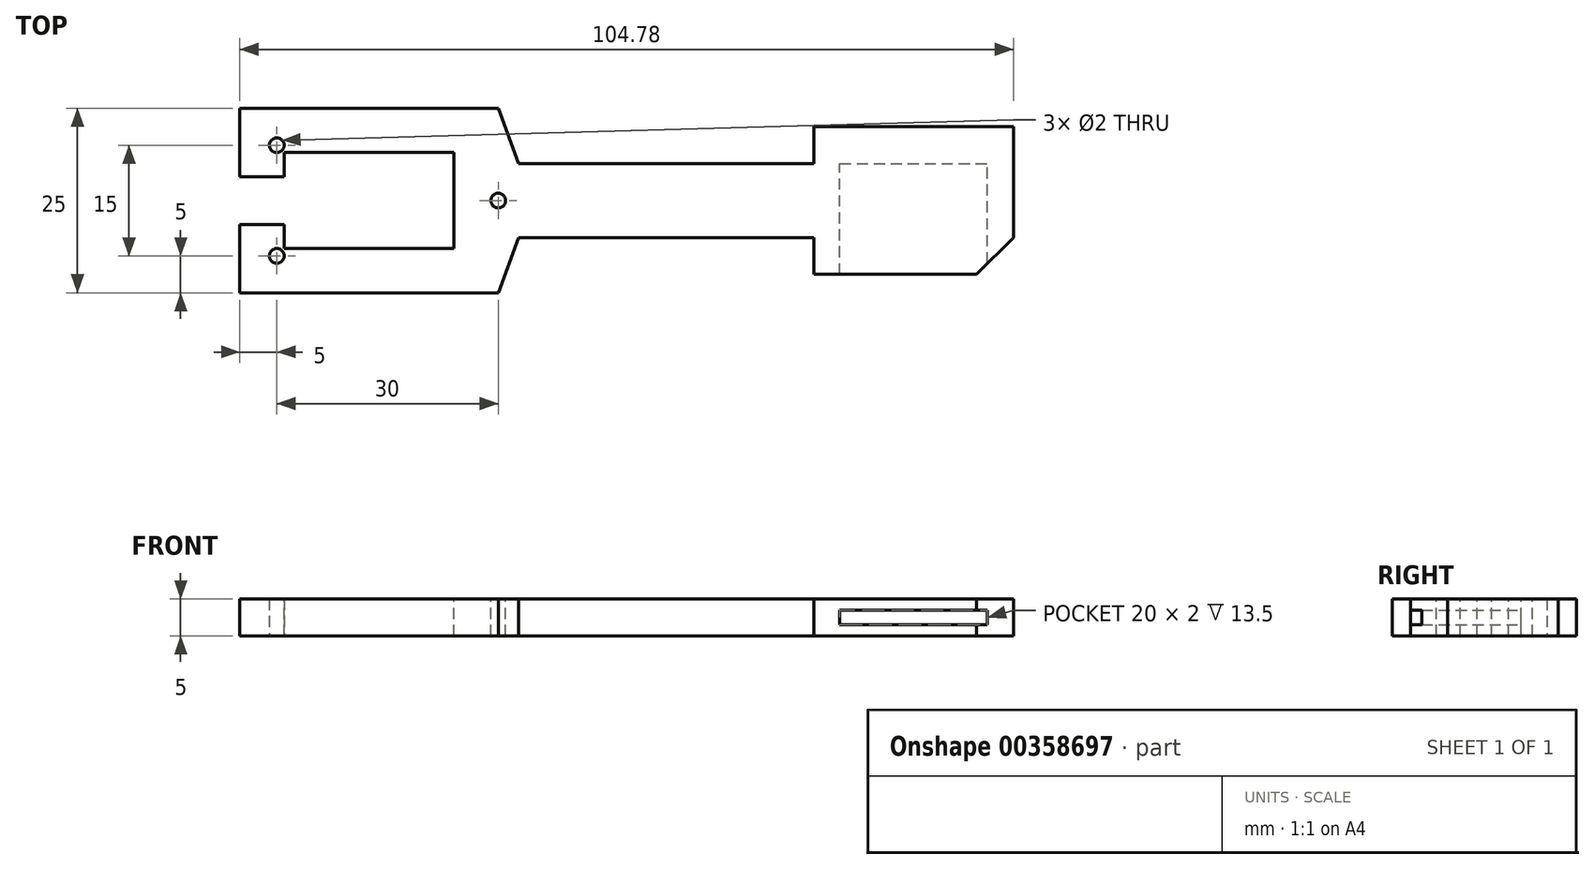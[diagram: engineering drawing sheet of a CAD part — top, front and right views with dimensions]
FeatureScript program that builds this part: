
annotation { "Feature Type Name" : "Feature", "Feature Type Description" : "" }
export const myFeature = defineFeature(function(context is Context, id is Id, definition is map)
    precondition{}
    {
        {
            var Q0;
            Q0=qCreatedBy(makeId("Top.planeOp"),FACE);
            var sketch = newSketch(context, id + "F0", { "sketchPlane" : qUnion([Q0])});
            skLineSegment(sketch, "E0.bottom", {"start": v(0, 0) * mm, "end": v(-35, 0) * mm});
            skLineSegment(sketch, "E0.top", {"start": v(0, 25) * mm, "end": v(-35, 25) * mm});
            skLineSegment(sketch, "E0.right", {"start": v(-35, 0) * mm, "end": v(-35, 25) * mm});
            skPoint(sketch, "E0.middle", {"position": v(-17.5, 12.5) * mm});
            skLineSegment(sketch, "E1.bottom", {"start": v(-29, 6) * mm, "end": v(-6, 6) * mm});
            skLineSegment(sketch, "E1.top", {"start": v(-29, 19) * mm, "end": v(-6, 19) * mm});
            skLineSegment(sketch, "E1.left", {"start": v(-29, 6) * mm, "end": v(-29, 19) * mm});
            skLineSegment(sketch, "E1.right", {"start": v(-6, 6) * mm, "end": v(-6, 19) * mm});
            skLineSegment(sketch, "E2", {"start": v(0, 25) * mm, "end": v(2.78, 17.5) * mm});
            skLineSegment(sketch, "E3", {"start": v(0, 0) * mm, "end": v(2.78, 7.5) * mm});
            skLineSegment(sketch, "E4", {"start": v(-17.5, 25) * mm, "end": v(-17.5, 19) * mm, "construction": true});
            skLineSegment(sketch, "E5", {"start": v(-17.5, 19) * mm, "end": v(-17.5, 12.5) * mm, "construction": true});
            skLineSegment(sketch, "E6", {"start": v(-17.5, 6) * mm, "end": v(-17.5, 0) * mm, "construction": true});
            skLineSegment(sketch, "E7", {"start": v(-17.5, 12.5) * mm, "end": v(-17.5, 6) * mm, "construction": true});
            skLineSegment(sketch, "E8", {"start": v(-6, 12.5) * mm, "end": v(2.78, 12.5) * mm, "construction": true});
            skLineSegment(sketch, "E9", {"start": v(2.78, 17.5) * mm, "end": v(42.78, 17.5) * mm});
            skLineSegment(sketch, "E10", {"start": v(42.78, 17.5) * mm, "end": v(42.78, 7.5) * mm});
            skLineSegment(sketch, "E11", {"start": v(42.78, 7.5) * mm, "end": v(2.78, 7.5) * mm});
            skLineSegment(sketch, "E12", {"start": v(2.78, 17.5) * mm, "end": v(2.78, 7.5) * mm});
            skLineSegment(sketch, "E13", {"start": v(42.78, 7.5) * mm, "end": v(42.78, 2.5) * mm});
            skLineSegment(sketch, "E14", {"start": v(42.78, 2.5) * mm, "end": v(64.78, 2.5) * mm});
            skLineSegment(sketch, "E15", {"start": v(64.78, 2.5) * mm, "end": v(69.78, 7.5) * mm});
            skLineSegment(sketch, "E16", {"start": v(69.78, 7.5) * mm, "end": v(69.78, 17.5) * mm});
            skLineSegment(sketch, "E17", {"start": v(42.78, 17.5) * mm, "end": v(42.78, 22.5) * mm});
            skLineSegment(sketch, "E18", {"start": v(42.78, 22.5) * mm, "end": v(69.78, 22.5) * mm});
            skLineSegment(sketch, "E19", {"start": v(69.78, 22.5) * mm, "end": v(69.78, 17.5) * mm});
            skLineSegment(sketch, "E20", {"start": v(42.78, 17.5) * mm, "end": v(57.78, 17.5) * mm});
            skLineSegment(sketch, "E21", {"start": v(57.78, 17.5) * mm, "end": v(57.78, 2.5) * mm});
            skLineSegment(sketch, "E22", {"start": v(57.78, 17.5) * mm, "end": v(57.78, 22.5) * mm});
            skLineSegment(sketch, "E23", {"start": v(57.78, 17.5) * mm, "end": v(69.78, 17.5) * mm});
            skPoint(sketch, "E24", {"position": v(-30, 20) * mm});
            skPoint(sketch, "E25", {"position": v(-30, 5) * mm});
            skLineSegment(sketch, "E26", {"start": v(-29, 15.75) * mm, "end": v(-35, 15.75) * mm});
            skPoint(sketch, "E26.startSnap0", {"position": v(-17.5, 15.75) * mm});
            skLineSegment(sketch, "E27", {"start": v(-29, 9.25) * mm, "end": v(-35, 9.25) * mm});
            skLineSegment(sketch, "E28", {"start": v(-29, 9.25) * mm, "end": v(-17.5, 9.25) * mm});
            skPoint(sketch, "E29", {"position": v(0, 12.5) * mm});
            skSolve(sketch);
        }
        {
            var Q0;
            Q0=makeQuery(id+"F0.imprint","IMPRINT",FACE,{"disambiguationData":[TD([[makeQuery(id+"F0.imprint","IMPRINT",EDGE,{"derivedFrom":sQuery(id+"F0.wireOp",EDGE,"E0.bottom")}),-1.0]])]});
            var Q1;
            Q1=makeQuery(id+"F0.imprint","IMPRINT",FACE,{"disambiguationData":[TD([[makeQuery(id+"F0.imprint","IMPRINT",EDGE,{"derivedFrom":sQuery(id+"F0.wireOp",EDGE,"E9")}),-1.0]])]});
            extrude(context, id + "F1", {"entities" : qUnion([Q0, Q1]), "oppositeDirection" : true, "depth" : 5 * mm, "symmetric" : true});
        }
        {
            var Q0;
            {var subQ0=sQuery(id+"F0.wireOp",EDGE,"E17");Q0=makeQuery(id+"F0.imprint","IMPRINT",FACE,{"disambiguationData":[TD([[makeQuery(id+"F0.imprint","IMPRINT",EDGE,{"derivedFrom":subQ0}),-1.0]])]});}
            var Q1;
            {var subQ0=sQuery(id+"F0.wireOp",EDGE,"E19");Q1=makeQuery(id+"F0.imprint","IMPRINT",FACE,{"disambiguationData":[TD([[makeQuery(id+"F0.imprint","IMPRINT",EDGE,{"derivedFrom":subQ0}),-1.0]])]});}
            var Q2;
            {var subQ1=sQuery(id+"F0.wireOp",EDGE,"E15");Q2=makeQuery(id+"F0.imprint","IMPRINT",FACE,{"disambiguationData":[TD([[makeQuery(id+"F0.imprint","IMPRINT",EDGE,{"derivedFrom":subQ1}),1.0]])]});}
            var Q3;
            Q3=makeQuery(id+"F0.imprint","IMPRINT",FACE,{"disambiguationData":[TD([[makeQuery(id+"F0.imprint","IMPRINT",EDGE,{"derivedFrom":sQuery(id+"F0.wireOp",EDGE,"E10")}),1.0]])]});
            extrude(context, id + "F2", {"entities" : qUnion([Q0, Q1, Q2, Q3]), "operationType" : NewBodyOperationType.ADD, "oppositeDirection" : true, "depth" : 5 * mm, "symmetric" : true});
        }
        {
            var Q0;
            Q0=makeQuery(id+"F2.opExtrude","SWEPT_FACE",FACE,{"disambiguationData":[OSD([sQuery(id+"F0.wireOp",EDGE,"E18")])]});
            var sketch = newSketch(context, id + "F3", { "sketchPlane" : qUnion([Q0])});
            skLineSegment(sketch, "E30.0.0", {"start": v(-42.78, 2.5) * mm, "end": v(-69.78, 2.5) * mm});
            skLineSegment(sketch, "E30.0.1", {"start": v(-69.78, 2.5) * mm, "end": v(-69.78, -2.5) * mm});
            skLineSegment(sketch, "E30.0.2", {"start": v(-69.78, -2.5) * mm, "end": v(-42.78, -2.5) * mm});
            skLineSegment(sketch, "E30.0.3", {"start": v(-42.78, -2.5) * mm, "end": v(-42.78, 2.5) * mm});
            skLineSegment(sketch, "E31.0", {"start": v(-46.28, -1) * mm, "end": v(-66.28, -1) * mm});
            skLineSegment(sketch, "E31.1", {"start": v(-46.28, -1) * mm, "end": v(-46.28, 1) * mm});
            skLineSegment(sketch, "E31.2", {"start": v(-66.28, 1) * mm, "end": v(-46.28, 1) * mm});
            skLineSegment(sketch, "E31.3", {"start": v(-66.28, 1) * mm, "end": v(-66.28, -1) * mm});
            skSolve(sketch);
        }
        {
            var Q0;
            Q0=makeQuery(id+"F3.imprint","IMPRINT",FACE,{"disambiguationData":[TD([[makeQuery(id+"F3.imprint","IMPRINT",EDGE,{"derivedFrom":sQuery(id+"F3.wireOp",EDGE,"E31.0")}),-1.0]])]});
            extrude(context, id + "F4", {"entities" : qUnion([Q0]), "operationType" : NewBodyOperationType.REMOVE, "oppositeDirection" : true, "depth" : 25 * mm});
        }
        {
            var Q0;
            Q0=sQuery(id+"F0.wireOp",VERTEX,"E24");
            var Q1;
            Q1=sQuery(id+"F0.wireOp",VERTEX,"E25");
            var Q2;
            Q2=makeQuery(id+"F1.opExtrude","SWEPT_BODY",BODY,{"disambiguationData":[OSD([sQuery(id+"F0.wireOp",EDGE,"E0.bottom"),sQuery(id+"F0.wireOp",EDGE,"E0.top"),sQuery(id+"F0.wireOp",EDGE,"E0.right"),sQuery(id+"F0.wireOp",EDGE,"E1.bottom"),sQuery(id+"F0.wireOp",EDGE,"E1.top"),sQuery(id+"F0.wireOp",EDGE,"E1.left"),sQuery(id+"F0.wireOp",EDGE,"E1.right"),sQuery(id+"F0.wireOp",EDGE,"E2"),sQuery(id+"F0.wireOp",EDGE,"E3"),sQuery(id+"F0.wireOp",EDGE,"E9"),sQuery(id+"F0.wireOp",EDGE,"E10"),sQuery(id+"F0.wireOp",EDGE,"E11")])]});
            hole(context, id + "F5", {"style" : HoleStyle.SIMPLE, "endStyle" : HoleEndStyle.BLIND, "oppositeDirection" : true, "holeDiameter" : 2 * mm, "holeDepth" : 30 * mm, "isTappedThrough" : true, "tappedDepth" : 12 * mm, "tapClearance" : 3, "locations" : qUnion([Q0, Q1]), "scope" : qUnion([Q2])});
        }
        {
            var Q0;
            Q0=sQuery(id+"F0.wireOp",VERTEX,"E25");
            var Q1;
            Q1=sQuery(id+"F0.wireOp",VERTEX,"E24");
            var Q2;
            Q2=makeQuery(id+"F1.opExtrude","SWEPT_BODY",BODY,{"disambiguationData":[OSD([sQuery(id+"F0.wireOp",EDGE,"E0.bottom"),sQuery(id+"F0.wireOp",EDGE,"E0.top"),sQuery(id+"F0.wireOp",EDGE,"E0.right"),sQuery(id+"F0.wireOp",EDGE,"E1.bottom"),sQuery(id+"F0.wireOp",EDGE,"E1.top"),sQuery(id+"F0.wireOp",EDGE,"E1.left"),sQuery(id+"F0.wireOp",EDGE,"E1.right"),sQuery(id+"F0.wireOp",EDGE,"E2"),sQuery(id+"F0.wireOp",EDGE,"E3"),sQuery(id+"F0.wireOp",EDGE,"E9"),sQuery(id+"F0.wireOp",EDGE,"E10"),sQuery(id+"F0.wireOp",EDGE,"E11")])]});
            hole(context, id + "F6", {"style" : HoleStyle.SIMPLE, "endStyle" : HoleEndStyle.BLIND, "holeDiameter" : 2 * mm, "holeDepth" : 30 * mm, "isTappedThrough" : true, "tappedDepth" : 12 * mm, "tapClearance" : 3, "locations" : qUnion([Q0, Q1]), "scope" : qUnion([Q2])});
        }
        {
            var Q0;
            Q0=sQuery(id+"F0.wireOp",VERTEX,"E29");
            var Q1;
            Q1=makeQuery(id+"F1.opExtrude","SWEPT_BODY",BODY,{"disambiguationData":[OSD([sQuery(id+"F0.wireOp",EDGE,"E0.bottom"),sQuery(id+"F0.wireOp",EDGE,"E0.top"),sQuery(id+"F0.wireOp",EDGE,"E0.right"),sQuery(id+"F0.wireOp",EDGE,"E1.bottom"),sQuery(id+"F0.wireOp",EDGE,"E1.top"),sQuery(id+"F0.wireOp",EDGE,"E1.left"),sQuery(id+"F0.wireOp",EDGE,"E1.right"),sQuery(id+"F0.wireOp",EDGE,"E2"),sQuery(id+"F0.wireOp",EDGE,"E3"),sQuery(id+"F0.wireOp",EDGE,"E9"),sQuery(id+"F0.wireOp",EDGE,"E10"),sQuery(id+"F0.wireOp",EDGE,"E11"),sQuery(id+"F0.wireOp",EDGE,"E26"),sQuery(id+"F0.wireOp",EDGE,"E27")])]});
            hole(context, id + "F7", {"style" : HoleStyle.SIMPLE, "endStyle" : HoleEndStyle.BLIND, "holeDiameter" : 2 * mm, "holeDepth" : 30 * mm, "isTappedThrough" : true, "tappedDepth" : 12 * mm, "tapClearance" : 3, "locations" : qUnion([Q0]), "scope" : qUnion([Q1])});
        }
        {
            var Q0;
            Q0=sQuery(id+"F0.wireOp",VERTEX,"E29");
            var Q1;
            Q1=makeQuery(id+"F1.opExtrude","SWEPT_BODY",BODY,{"disambiguationData":[OSD([sQuery(id+"F0.wireOp",EDGE,"E0.bottom"),sQuery(id+"F0.wireOp",EDGE,"E0.top"),sQuery(id+"F0.wireOp",EDGE,"E0.right"),sQuery(id+"F0.wireOp",EDGE,"E1.bottom"),sQuery(id+"F0.wireOp",EDGE,"E1.top"),sQuery(id+"F0.wireOp",EDGE,"E1.left"),sQuery(id+"F0.wireOp",EDGE,"E1.right"),sQuery(id+"F0.wireOp",EDGE,"E2"),sQuery(id+"F0.wireOp",EDGE,"E3"),sQuery(id+"F0.wireOp",EDGE,"E9"),sQuery(id+"F0.wireOp",EDGE,"E10"),sQuery(id+"F0.wireOp",EDGE,"E11"),sQuery(id+"F0.wireOp",EDGE,"E26"),sQuery(id+"F0.wireOp",EDGE,"E27")])]});
            hole(context, id + "F8", {"style" : HoleStyle.SIMPLE, "endStyle" : HoleEndStyle.BLIND, "oppositeDirection" : true, "holeDiameter" : 2 * mm, "holeDepth" : 30 * mm, "isTappedThrough" : true, "tappedDepth" : 12 * mm, "tapClearance" : 3, "locations" : qUnion([Q0]), "scope" : qUnion([Q1])});
        }
        {
            var Q0;
            Q0=makeQuery(id+"F3.imprint","IMPRINT",FACE,{"disambiguationData":[TD([[makeQuery(id+"F3.imprint","IMPRINT",EDGE,{"derivedFrom":sQuery(id+"F3.wireOp",EDGE,"E31.0")}),-1.0]])]});
            extrude(context, id + "F9", {"entities" : qUnion([Q0]), "operationType" : NewBodyOperationType.ADD, "oppositeDirection" : true, "depth" : 5 * mm});
        }
    });
